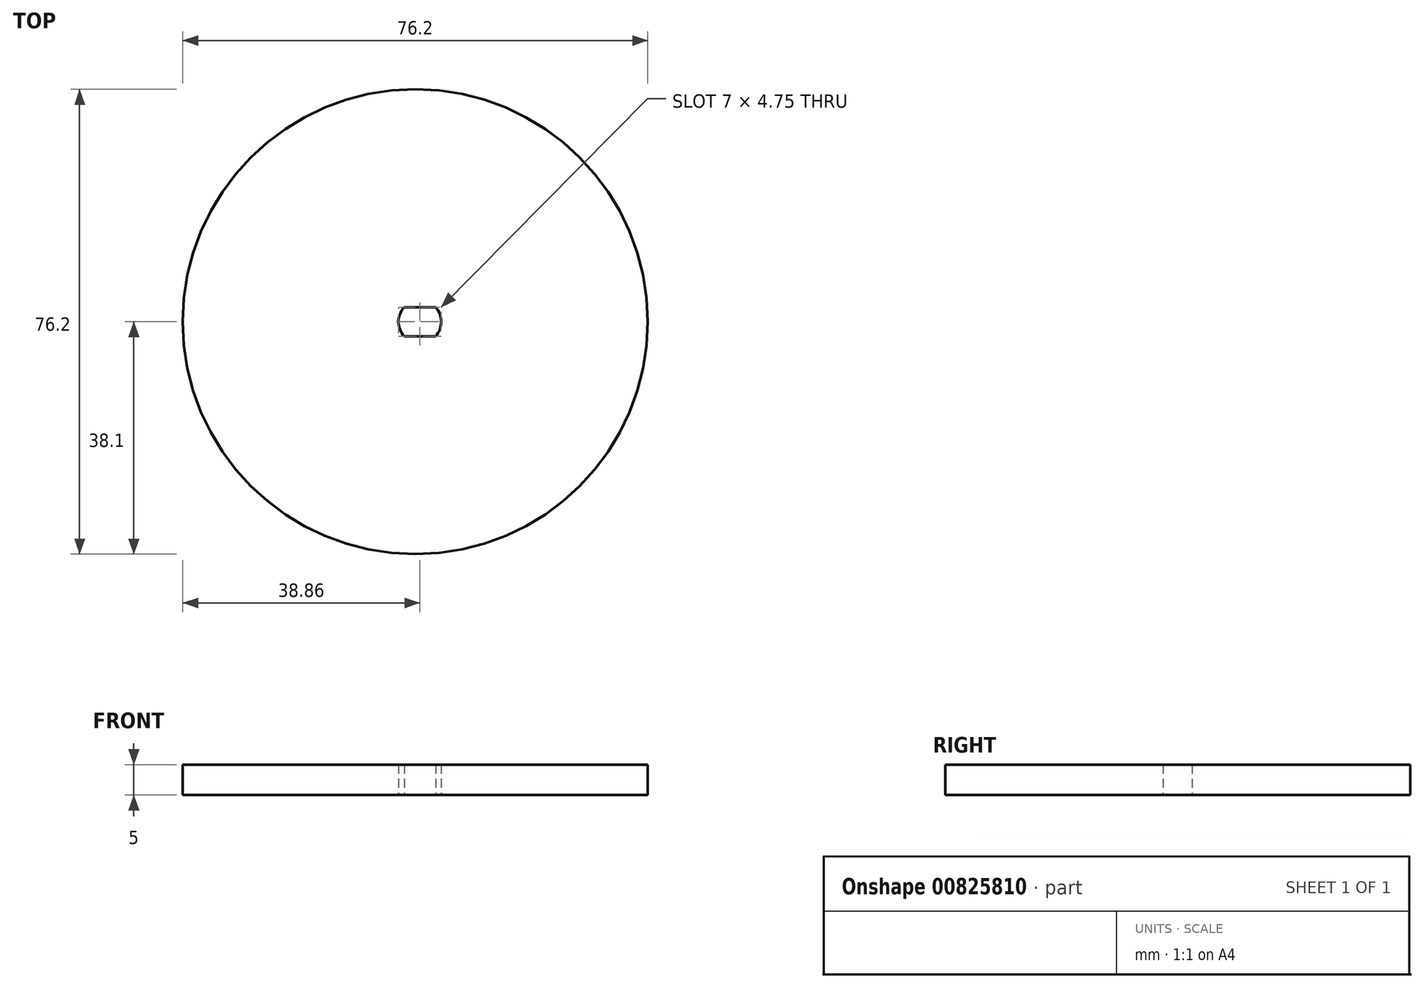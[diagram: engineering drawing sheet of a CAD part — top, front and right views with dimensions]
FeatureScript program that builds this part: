
annotation { "Feature Type Name" : "Feature", "Feature Type Description" : "" }
export const myFeature = defineFeature(function(context is Context, id is Id, definition is map)
    precondition{}
    {
        {
            var Q0;
            Q0=qCreatedBy(makeId("Top.planeOp"),FACE);
            var sketch = newSketch(context, id + "F0", { "sketchPlane" : qUnion([Q0])});
            skCircle(sketch, "E0", {"center": v(0, 0) * mm, "radius": 3.5 * mm});
            skLineSegment(sketch, "E1", {"start": v(0.87, 0) * mm, "end": v(3.5, 0) * mm, "construction": true});
            skLineSegment(sketch, "E2", {"start": v(-2.57, 2.38) * mm, "end": v(2.57, 2.38) * mm});
            skLineSegment(sketch, "E3.MirrorCS", {"start": v(-2.57, -2.37) * mm, "end": v(2.57, -2.37) * mm});
            skCircle(sketch, "E4", {"center": v(-0.76, 0) * mm, "radius": 38.1 * mm});
            skSolve(sketch);
        }
        {
            var Q0;
            {var subQ0=sQuery(id+"F0.wireOp",EDGE,"E2");Q0=makeQuery(id+"F0.imprint","IMPRINT",FACE,{"disambiguationData":[TD([[makeQuery(id+"F0.imprint","IMPRINT",EDGE,{"derivedFrom":subQ0}),1.0]])]});}
            var Q1;
            {var subQ0=sQuery(id+"F0.wireOp",EDGE,"E3.MirrorCS");Q1=makeQuery(id+"F0.imprint","IMPRINT",FACE,{"disambiguationData":[TD([[makeQuery(id+"F0.imprint","IMPRINT",EDGE,{"derivedFrom":subQ0}),-1.0]])]});}
            var Q2;
            Q2=makeQuery(id+"F0.imprint","IMPRINT",FACE,{"disambiguationData":[TD([[makeQuery(id+"F0.imprint","IMPRINT",EDGE,{"derivedFrom":sQuery(id+"F0.wireOp",EDGE,"E4")}),1.0]])]});
            extrude(context, id + "F1", {"entities" : qUnion([Q0, Q1, Q2]), "depth" : 5 * mm, "offsetDistance" : 25 * mm});
        }
    });
